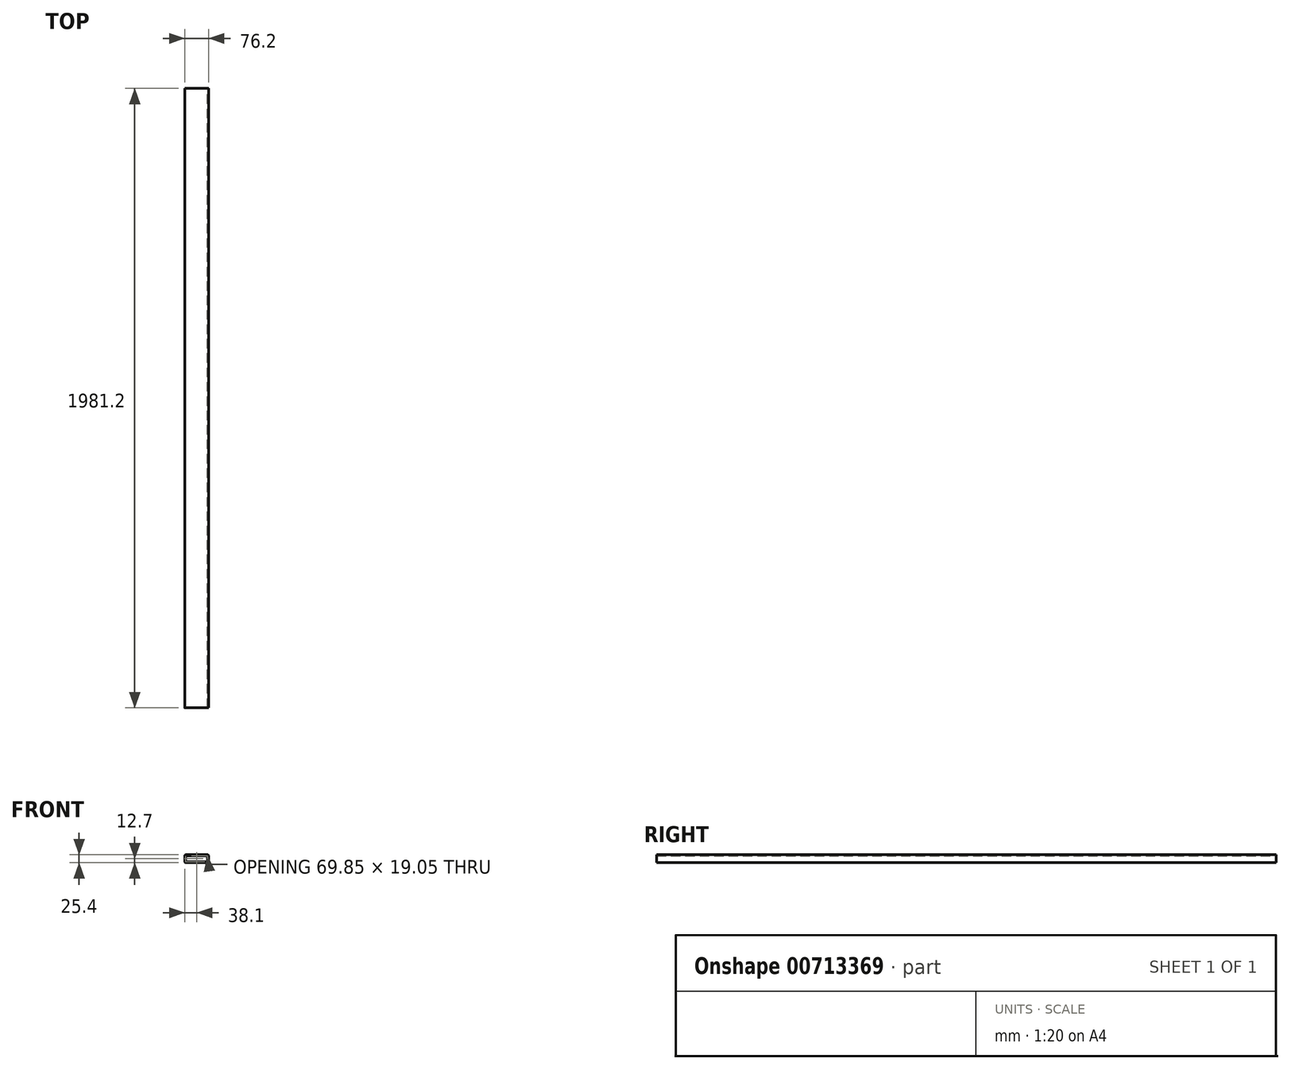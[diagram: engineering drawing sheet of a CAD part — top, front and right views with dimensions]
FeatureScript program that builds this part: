
annotation { "Feature Type Name" : "Feature", "Feature Type Description" : "" }
export const myFeature = defineFeature(function(context is Context, id is Id, definition is map)
    precondition{}
    {
        {
            var Q0;
            Q0=qCreatedBy(makeId("Front.planeOp"),FACE);
            var sketch = newSketch(context, id + "F0", { "sketchPlane" : qUnion([Q0])});
            skLineSegment(sketch, "E0.bottom", {"start": v(3.18, 0) * mm, "end": v(73.02, 0) * mm});
            skLineSegment(sketch, "E0.top", {"start": v(3.18, 25.4) * mm, "end": v(73.02, 25.4) * mm});
            skLineSegment(sketch, "E0.left", {"start": v(0, 3.18) * mm, "end": v(0, 22.22) * mm});
            skLineSegment(sketch, "E0.right", {"start": v(76.2, 3.18) * mm, "end": v(76.2, 22.22) * mm});
            skLineSegment(sketch, "E1.bottom", {"start": v(6.35, 3.17) * mm, "end": v(69.85, 3.17) * mm});
            skLineSegment(sketch, "E1.top", {"start": v(6.35, 22.23) * mm, "end": v(69.85, 22.23) * mm});
            skLineSegment(sketch, "E1.left", {"start": v(3.17, 6.35) * mm, "end": v(3.17, 19.05) * mm});
            skLineSegment(sketch, "E1.right", {"start": v(73.03, 6.35) * mm, "end": v(73.03, 19.05) * mm});
            skPoint(sketch, "E2.visualSharp", {"position": v(0, 25.4) * mm});
            skArc(sketch, "E2.filletArc", {"start": v(3.17, 25.4) * mm, "mid": v(0.93, 24.47) * mm, "end": v(0, 22.23) * mm});
            skArc(sketch, "E3.filletArc", {"start": v(6.35, 22.23) * mm, "mid": v(4.1, 21.3) * mm, "end": v(3.17, 19.05) * mm});
            skPoint(sketch, "E4.visualSharp", {"position": v(3.17, 3.18) * mm});
            skArc(sketch, "E4.filletArc", {"start": v(3.17, 6.35) * mm, "mid": v(4.1, 4.1) * mm, "end": v(6.35, 3.17) * mm});
            skPoint(sketch, "E5.visualSharp", {"position": v(0, 0) * mm});
            skArc(sketch, "E5.filletArc", {"start": v(0, 3.18) * mm, "mid": v(0.93, 0.93) * mm, "end": v(3.18, 0) * mm});
            skPoint(sketch, "E6.visualSharp", {"position": v(73.03, 22.23) * mm});
            skArc(sketch, "E6.filletArc", {"start": v(73.03, 19.05) * mm, "mid": v(72.1, 21.3) * mm, "end": v(69.85, 22.23) * mm});
            skPoint(sketch, "E7.visualSharp", {"position": v(76.2, 25.4) * mm});
            skArc(sketch, "E7.filletArc", {"start": v(76.2, 22.22) * mm, "mid": v(75.27, 24.47) * mm, "end": v(73.02, 25.4) * mm});
            skPoint(sketch, "E8.visualSharp", {"position": v(73.03, 3.17) * mm});
            skArc(sketch, "E8.filletArc", {"start": v(69.85, 3.17) * mm, "mid": v(72.1, 4.1) * mm, "end": v(73.03, 6.35) * mm});
            skPoint(sketch, "E9.visualSharp", {"position": v(76.2, 0) * mm});
            skArc(sketch, "E9.filletArc", {"start": v(73.02, 0) * mm, "mid": v(75.27, 0.93) * mm, "end": v(76.2, 3.18) * mm});
            skSolve(sketch);
        }
        {
            var Q0;
            Q0 = qSketchRegion(id + "F0", true);
            extrude(context, id + "F1", {"entities" : qUnion([Q0]), "depth" : 1981.2 * mm, "offsetDistance" : 25.4 * mm});
        }
    });
